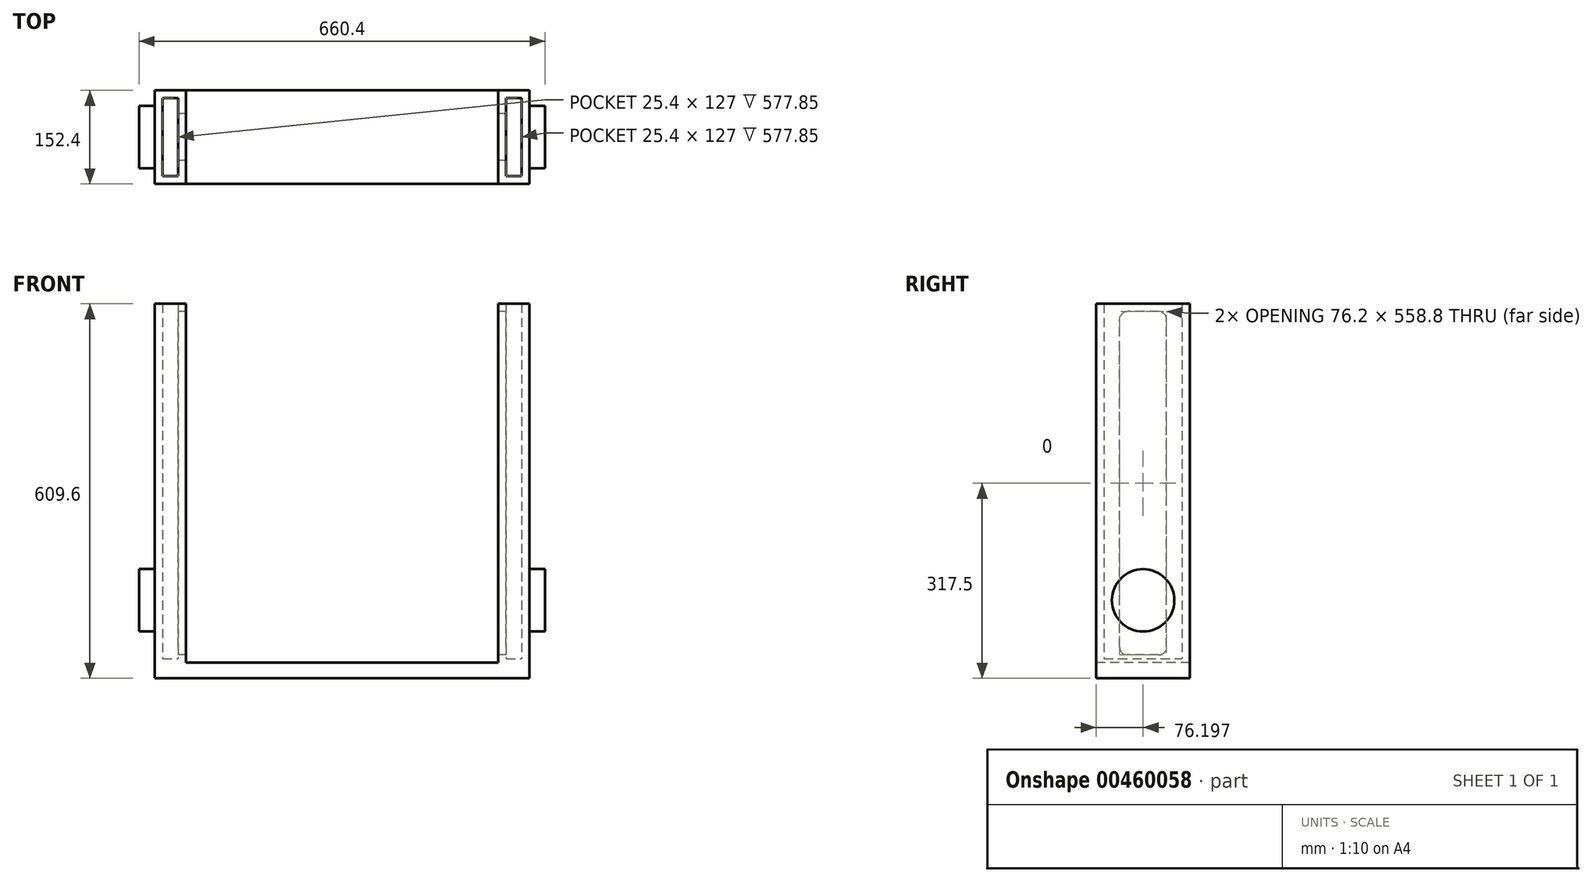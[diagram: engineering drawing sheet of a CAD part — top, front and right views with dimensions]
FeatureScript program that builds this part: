
annotation { "Feature Type Name" : "Feature", "Feature Type Description" : "" }
export const myFeature = defineFeature(function(context is Context, id is Id, definition is map)
    precondition{}
    {
        {
            var Q0;
            Q0=qCreatedBy(makeId("Top.planeOp"),FACE);
            var sketch = newSketch(context, id + "F0", { "sketchPlane" : qUnion([Q0])});
            skLineSegment(sketch, "E0.bottom", {"start": v(-105.94, 16.4) * mm, "end": v(-55.14, 16.4) * mm});
            skLineSegment(sketch, "E0.top", {"start": v(-105.94, -136) * mm, "end": v(-55.14, -136) * mm});
            skLineSegment(sketch, "E0.left", {"start": v(-105.94, 16.4) * mm, "end": v(-105.94, -136) * mm});
            skLineSegment(sketch, "E0.right", {"start": v(-55.14, 16.4) * mm, "end": v(-55.14, -136) * mm});
            skLineSegment(sketch, "E1.bottom", {"start": v(-93.24, -123.3) * mm, "end": v(-67.84, -123.3) * mm});
            skLineSegment(sketch, "E1.top", {"start": v(-93.24, 3.7) * mm, "end": v(-67.84, 3.7) * mm});
            skLineSegment(sketch, "E1.left", {"start": v(-93.24, -123.3) * mm, "end": v(-93.24, 3.7) * mm});
            skLineSegment(sketch, "E1.right", {"start": v(-67.84, -123.3) * mm, "end": v(-67.84, 3.7) * mm});
            skLineSegment(sketch, "E2", {"start": v(-55.14, 16.4) * mm, "end": v(452.86, 16.4) * mm});
            skLineSegment(sketch, "E3", {"start": v(-55.14, -136) * mm, "end": v(452.86, -136) * mm});
            skLineSegment(sketch, "E4", {"start": v(452.86, -136) * mm, "end": v(452.86, 16.4) * mm});
            skLineSegment(sketch, "E5", {"start": v(452.86, 16.4) * mm, "end": v(452.86, 16.4) * mm});
            skLineSegment(sketch, "E6", {"start": v(452.86, 16.4) * mm, "end": v(503.66, 16.4) * mm});
            skLineSegment(sketch, "E7", {"start": v(503.66, 16.4) * mm, "end": v(503.66, -136) * mm});
            skLineSegment(sketch, "E8", {"start": v(503.66, -136) * mm, "end": v(452.86, -136) * mm});
            skLineSegment(sketch, "E9", {"start": v(452.86, -136) * mm, "end": v(452.86, -136) * mm});
            skLineSegment(sketch, "E10.bottom", {"start": v(465.56, -123.3) * mm, "end": v(490.96, -123.3) * mm});
            skLineSegment(sketch, "E10.top", {"start": v(465.56, 3.7) * mm, "end": v(490.96, 3.7) * mm});
            skLineSegment(sketch, "E10.left", {"start": v(465.56, -123.3) * mm, "end": v(465.56, 3.7) * mm});
            skLineSegment(sketch, "E10.right", {"start": v(490.96, -123.3) * mm, "end": v(490.96, 3.7) * mm});
            skSolve(sketch);
        }
        {
            var Q0;
            Q0=makeQuery(id+"F0.imprint","IMPRINT",FACE,{"disambiguationData":[TD([[makeQuery(id+"F0.imprint","IMPRINT",EDGE,{"derivedFrom":sQuery(id+"F0.wireOp",EDGE,"E1.bottom")}),1.0]])]});
            extrude(context, id + "F1", {"entities" : qUnion([Q0]), "depth" : 31.75 * mm});
        }
        {
            var Q0;
            Q0=makeQuery(id+"F0.imprint","IMPRINT",FACE,{"disambiguationData":[TD([[makeQuery(id+"F0.imprint","IMPRINT",EDGE,{"derivedFrom":sQuery(id+"F0.wireOp",EDGE,"E0.bottom")}),-1.0]])]});
            extrude(context, id + "F2", {"entities" : qUnion([Q0]), "operationType" : NewBodyOperationType.ADD, "depth" : 609.6 * mm});
        }
        {
            var Q0;
            {var subQ0=sQuery(id+"F0.wireOp",EDGE,"E2");Q0=makeQuery(id+"F0.imprint","IMPRINT",FACE,{"disambiguationData":[TD([[makeQuery(id+"F0.imprint","IMPRINT",EDGE,{"derivedFrom":subQ0}),-1.0]])]});}
            extrude(context, id + "F3", {"entities" : qUnion([Q0]), "operationType" : NewBodyOperationType.ADD, "depth" : 25.4 * mm});
        }
        {
            var Q0;
            Q0=makeQuery(id+"F0.imprint","IMPRINT",FACE,{"disambiguationData":[TD([[makeQuery(id+"F0.imprint","IMPRINT",EDGE,{"derivedFrom":sQuery(id+"F0.wireOp",EDGE,"E4")}),-1.0]])]});
            extrude(context, id + "F4", {"entities" : qUnion([Q0]), "operationType" : NewBodyOperationType.ADD, "depth" : 609.6 * mm});
        }
        {
            var Q0;
            Q0=makeQuery(id+"F0.imprint","IMPRINT",FACE,{"disambiguationData":[TD([[makeQuery(id+"F0.imprint","IMPRINT",EDGE,{"derivedFrom":sQuery(id+"F0.wireOp",EDGE,"E10.bottom")}),1.0]])]});
            extrude(context, id + "F5", {"entities" : qUnion([Q0]), "operationType" : NewBodyOperationType.ADD, "depth" : 31.75 * mm});
        }
        {
            var Q0;
            Q0=makeQuery(id+"F4.opExtrude","SWEPT_FACE",FACE,{"disambiguationData":[OSD([sQuery(id+"F0.wireOp",EDGE,"E4")])]});
            var sketch = newSketch(context, id + "F6", { "sketchPlane" : qUnion([Q0])});
            skLineSegment(sketch, "E11.bottom", {"start": v(21.7, 38.1) * mm, "end": v(97.9, 38.1) * mm});
            skLineSegment(sketch, "E11.top", {"start": v(21.7, 596.9) * mm, "end": v(97.9, 596.9) * mm});
            skLineSegment(sketch, "E11.left", {"start": v(21.7, 38.1) * mm, "end": v(21.7, 596.9) * mm});
            skLineSegment(sketch, "E11.right", {"start": v(97.9, 38.1) * mm, "end": v(97.9, 596.9) * mm});
            skSolve(sketch);
        }
        {
            var Q0;
            Q0 = qSketchRegion(id + "F6", true);
            extrude(context, id + "F7", {"entities" : qUnion([Q0]), "operationType" : NewBodyOperationType.REMOVE, "oppositeDirection" : true, "depth" : 25.4 * mm, "hasSecondDirection" : true, "secondDirectionOppositeDirection" : false, "secondDirectionDepth" : 533.4 * mm});
        }
        {
            var Q0;
            {var subQ0=sQuery(id+"F6.wireOp",EDGE,"E11.bottom");var subQ1=sQuery(id+"F6.wireOp",EDGE,"E11.right");Q0=makeQuery(id+"F7.boolean.opBoolean","COPY",EDGE,{"disambiguationData":[TD([makeQuery(id+"F4.opExtrude","SWEPT_FACE",FACE,{"disambiguationData":[OSD([sQuery(id+"F0.wireOp",EDGE,"E4")])]})])],"derivedFrom":makeQuery(id+"F7.opExtrude","SWEPT_EDGE",EDGE,{"disambiguationData":[OSD([subQ0,subQ1])]})});}
            var Q1;
            {var subQ0=sQuery(id+"F6.wireOp",EDGE,"E11.bottom");var subQ1=sQuery(id+"F6.wireOp",EDGE,"E11.left");Q1=makeQuery(id+"F7.boolean.opBoolean","COPY",EDGE,{"disambiguationData":[TD([makeQuery(id+"F4.opExtrude","SWEPT_FACE",FACE,{"disambiguationData":[OSD([sQuery(id+"F0.wireOp",EDGE,"E4")])]})])],"derivedFrom":makeQuery(id+"F7.opExtrude","SWEPT_EDGE",EDGE,{"disambiguationData":[OSD([subQ0,subQ1])]})});}
            var Q2;
            {var subQ0=sQuery(id+"F6.wireOp",EDGE,"E11.right");var subQ1=sQuery(id+"F6.wireOp",EDGE,"E11.top");Q2=makeQuery(id+"F7.boolean.opBoolean","COPY",EDGE,{"disambiguationData":[TD([makeQuery(id+"F4.opExtrude","SWEPT_FACE",FACE,{"disambiguationData":[OSD([sQuery(id+"F0.wireOp",EDGE,"E4")])]})])],"derivedFrom":makeQuery(id+"F7.opExtrude","SWEPT_EDGE",EDGE,{"disambiguationData":[OSD([subQ1,subQ0])]})});}
            var Q3;
            {var subQ0=sQuery(id+"F6.wireOp",EDGE,"E11.top");var subQ1=sQuery(id+"F6.wireOp",EDGE,"E11.left");Q3=makeQuery(id+"F7.boolean.opBoolean","COPY",EDGE,{"disambiguationData":[TD([makeQuery(id+"F4.opExtrude","SWEPT_FACE",FACE,{"disambiguationData":[OSD([sQuery(id+"F0.wireOp",EDGE,"E4")])]})])],"derivedFrom":makeQuery(id+"F7.opExtrude","SWEPT_EDGE",EDGE,{"disambiguationData":[OSD([subQ0,subQ1])]})});}
            var Q4;
            {var subQ0=sQuery(id+"F6.wireOp",EDGE,"E11.bottom");var subQ1=sQuery(id+"F6.wireOp",EDGE,"E11.left");Q4=makeQuery(id+"F7.boolean.opBoolean","COPY",EDGE,{"disambiguationData":[TD([makeQuery(id+"F2.opExtrude","SWEPT_FACE",FACE,{"disambiguationData":[OSD([sQuery(id+"F0.wireOp",EDGE,"E0.right")])]})])],"derivedFrom":makeQuery(id+"F7.opExtrude","SWEPT_EDGE",EDGE,{"disambiguationData":[OSD([subQ0,subQ1])]})});}
            var Q5;
            {var subQ0=sQuery(id+"F6.wireOp",EDGE,"E11.top");var subQ1=sQuery(id+"F6.wireOp",EDGE,"E11.left");Q5=makeQuery(id+"F7.boolean.opBoolean","COPY",EDGE,{"disambiguationData":[TD([makeQuery(id+"F2.opExtrude","SWEPT_FACE",FACE,{"disambiguationData":[OSD([sQuery(id+"F0.wireOp",EDGE,"E0.right")])]})])],"derivedFrom":makeQuery(id+"F7.opExtrude","SWEPT_EDGE",EDGE,{"disambiguationData":[OSD([subQ0,subQ1])]})});}
            var Q6;
            {var subQ0=sQuery(id+"F6.wireOp",EDGE,"E11.top");var subQ1=sQuery(id+"F6.wireOp",EDGE,"E11.right");Q6=makeQuery(id+"F7.boolean.opBoolean","COPY",EDGE,{"disambiguationData":[TD([makeQuery(id+"F2.opExtrude","SWEPT_FACE",FACE,{"disambiguationData":[OSD([sQuery(id+"F0.wireOp",EDGE,"E0.right")])]})])],"derivedFrom":makeQuery(id+"F7.opExtrude","SWEPT_EDGE",EDGE,{"disambiguationData":[OSD([subQ0,subQ1])]})});}
            var Q7;
            {var subQ0=sQuery(id+"F6.wireOp",EDGE,"E11.bottom");var subQ1=sQuery(id+"F6.wireOp",EDGE,"E11.right");Q7=makeQuery(id+"F7.boolean.opBoolean","COPY",EDGE,{"disambiguationData":[TD([makeQuery(id+"F2.opExtrude","SWEPT_FACE",FACE,{"disambiguationData":[OSD([sQuery(id+"F0.wireOp",EDGE,"E0.right")])]})])],"derivedFrom":makeQuery(id+"F7.opExtrude","SWEPT_EDGE",EDGE,{"disambiguationData":[OSD([subQ0,subQ1])]})});}
            fillet(context, id + "F8", {"entities" : qUnion([Q0, Q1, Q2, Q3, Q4, Q5, Q6, Q7]), "radius" : 12.7 * mm, "tangentPropagation" : true, "allowEdgeOverflow" : false});
        }
        {
            var Q0;
            Q0=makeQuery(id+"F2.opExtrude","SWEPT_FACE",FACE,{"disambiguationData":[OSD([sQuery(id+"F0.wireOp",EDGE,"E0.left")])]});
            var sketch = newSketch(context, id + "F9", { "sketchPlane" : qUnion([Q0])});
            skLineSegment(sketch, "E12", {"start": v(59.8, 0) * mm, "end": v(59.8, 127) * mm});
            skCircle(sketch, "E13", {"center": v(59.8, 127) * mm, "radius": 50.8 * mm});
            skSolve(sketch);
        }
        {
            var Q0;
            Q0 = qSketchRegion(id + "F9", true);
            extrude(context, id + "F10", {"entities" : qUnion([Q0]), "operationType" : NewBodyOperationType.ADD, "depth" : 25.4 * mm});
        }
        {
            var Q0;
            Q0=makeQuery(id+"F4.opExtrude","SWEPT_FACE",FACE,{"disambiguationData":[OSD([sQuery(id+"F0.wireOp",EDGE,"E7")])]});
            var sketch = newSketch(context, id + "F11", { "sketchPlane" : qUnion([Q0])});
            skLineSegment(sketch, "E14", {"start": v(-59.8, 0) * mm, "end": v(-59.8, 127) * mm});
            skCircle(sketch, "E15", {"center": v(-59.8, 127) * mm, "radius": 50.8 * mm});
            skSolve(sketch);
        }
        {
            var Q0;
            Q0=makeQuery(id+"F11.imprint","IMPRINT",FACE,{"disambiguationData":[TD([[makeQuery(id+"F11.imprint","IMPRINT",EDGE,{"derivedFrom":sQuery(id+"F11.wireOp",EDGE,"E15")}),1.0]])]});
            extrude(context, id + "F12", {"entities" : qUnion([Q0]), "operationType" : NewBodyOperationType.ADD, "depth" : 25.4 * mm});
        }
    });
